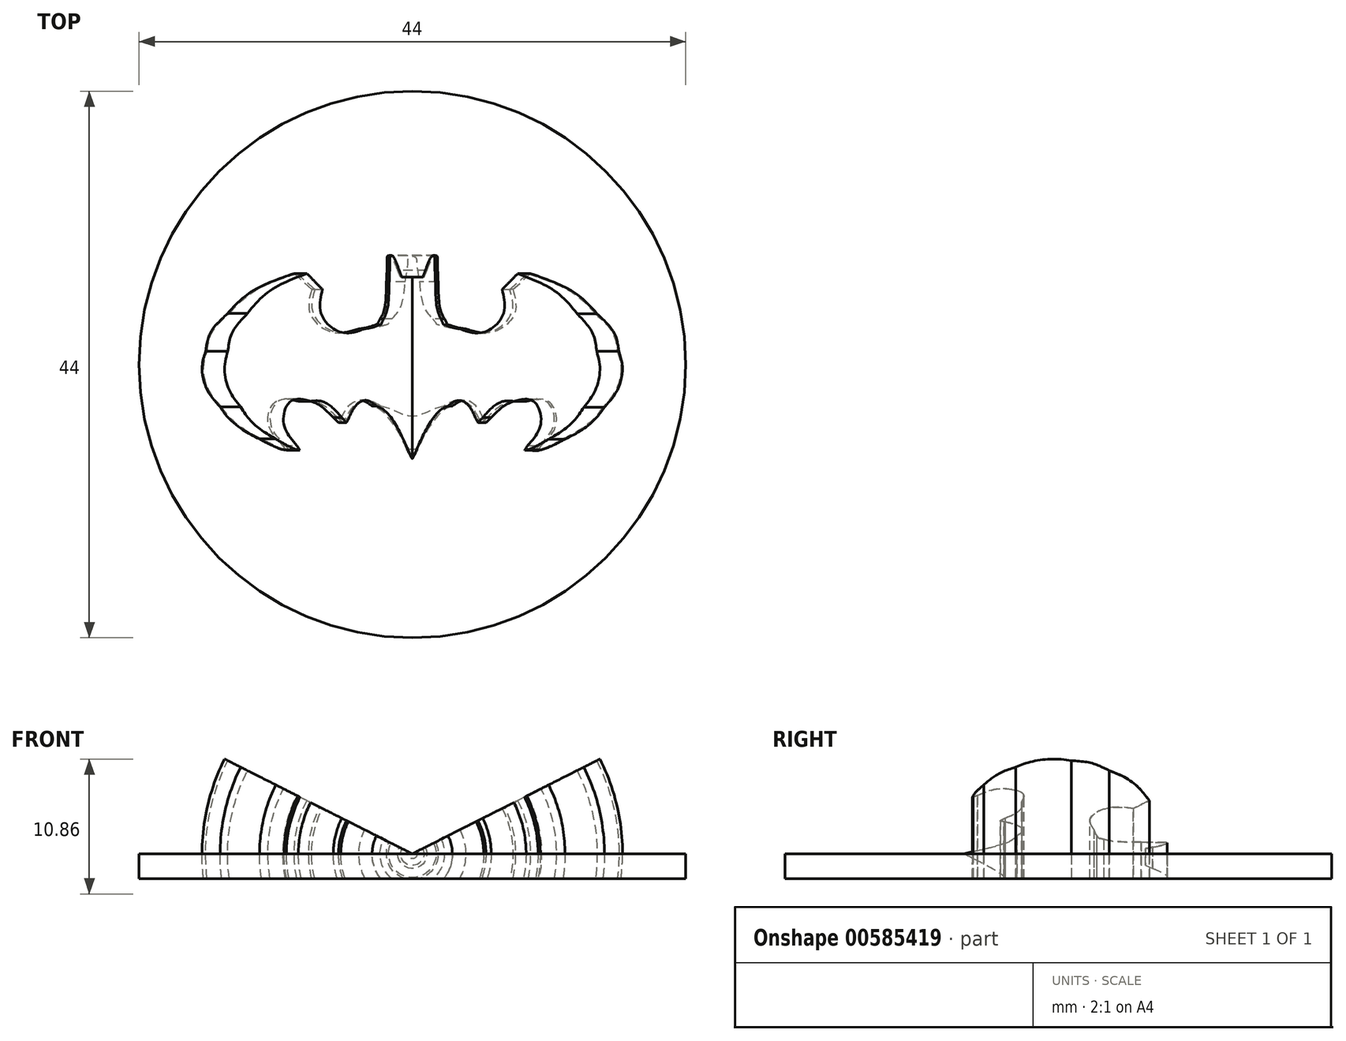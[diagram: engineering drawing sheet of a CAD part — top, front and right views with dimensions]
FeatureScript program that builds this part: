
annotation { "Feature Type Name" : "Feature", "Feature Type Description" : "" }
export const myFeature = defineFeature(function(context is Context, id is Id, definition is map)
    precondition{}
    {
        {
            var Q0;
            Q0=qCreatedBy(makeId("Top.planeOp"),FACE);
            var sketch = newSketch(context, id + "F0", { "sketchPlane" : qUnion([Q0])});
            skCircle(sketch, "E0", {"center": v(0, 0) * mm, "radius": 22 * mm});
            skSolve(sketch);
        }
        {
            var Q0;
            Q0=makeQuery(id+"F0.imprint","IMPRINT",FACE,{"disambiguationData":[TD([[makeQuery(id+"F0.imprint","IMPRINT",EDGE,{"derivedFrom":sQuery(id+"F0.wireOp",EDGE,"E0")}),1.0]])]});
            extrude(context, id + "F1", {"entities" : qUnion([Q0]), "depth" : 2 * mm, "offsetDistance" : 25 * mm});
        }
        {
            var Q0;
            Q0=makeQuery(id+"F1.opExtrude","CAP_FACE",FACE,{"disambiguationData":[OSD([sQuery(id+"F0.wireOp",EDGE,"E0")])],"isStart":false});
            var sketch = newSketch(context, id + "F2", { "sketchPlane" : qUnion([Q0])});
            skFitSpline(sketch, "E1", {"points": [v(-0.13, 10.66) * mm, v(-2.12, 10.65) * mm, v(-4.12, 10.46) * mm, v(-6.06, 10.08) * mm]});
            skFitSpline(sketch, "E2", {"points": [v(-6.06, 10.08) * mm, v(-12.64, 8.8) * mm, v(-17.56, 5.4) * mm, v(-18.46, 1.5) * mm]});
            skFitSpline(sketch, "E3", {"points": [v(-18.46, 1.5) * mm, v(-18.67, 0.6) * mm, v(-18.7, -0.04) * mm, v(-18.6, -0.8) * mm]});
            skFitSpline(sketch, "E4", {"points": [v(-18.6, -0.8) * mm, v(-18.34, -2.52) * mm, v(-17.58, -3.93) * mm, v(-16.12, -5.37) * mm]});
            skFitSpline(sketch, "E5", {"points": [v(-16.12, -5.37) * mm, v(-13.13, -8.34) * mm, v(-7.89, -10.27) * mm, v(-1.84, -10.64) * mm]});
            skFitSpline(sketch, "E6", {"points": [v(-1.84, -10.64) * mm, v(-0.97, -10.7) * mm, v(2.5, -10.62) * mm, v(3.31, -10.53) * mm]});
            skFitSpline(sketch, "E7", {"points": [v(3.31, -10.53) * mm, v(5.05, -10.33) * mm, v(5.92, -10.17) * mm, v(7.45, -9.8) * mm]});
            skFitSpline(sketch, "E8", {"points": [v(7.45, -9.8) * mm, v(14.92, -7.94) * mm, v(19.33, -3.65) * mm, v(18.58, 1.02) * mm]});
            skFitSpline(sketch, "E9", {"points": [v(18.58, 1.02) * mm, v(17.95, 4.88) * mm, v(13.66, 8.25) * mm, v(7.4, 9.79) * mm]});
            skFitSpline(sketch, "E10", {"points": [v(7.4, 9.79) * mm, v(5, 10.38) * mm, v(2.44, 10.67) * mm, v(-0.13, 10.66) * mm]});
            skFitSpline(sketch, "E11", {"points": [v(1.9, 8.75) * mm, v(1.97, 8.75) * mm, v(2.02, 8.14) * mm, v(2.07, 6.65) * mm]});
            skFitSpline(sketch, "E12", {"points": [v(2.07, 6.65) * mm, v(2.12, 5.3) * mm, v(2.3, 4.22) * mm, v(2.58, 3.66) * mm]});
            skFitSpline(sketch, "E13", {"points": [v(2.58, 3.66) * mm, v(2.8, 3.24) * mm, v(2.8, 3.24) * mm, v(3.23, 3.1) * mm]});
            skFitSpline(sketch, "E14", {"points": [v(3.23, 3.1) * mm, v(3.47, 3.01) * mm, v(3.95, 2.91) * mm, v(4.28, 2.87) * mm]});
            skFitSpline(sketch, "E15", {"points": [v(4.28, 2.87) * mm, v(6.43, 2.6) * mm, v(8.2, 4.07) * mm, v(8.1, 6.04) * mm]});
            skFitSpline(sketch, "E16", {"points": [v(7.51, 7.65) * mm, v(7.37, 7.83) * mm, v(7.26, 7.99) * mm, v(7.27, 8) * mm]});
            skFitSpline(sketch, "E17", {"points": [v(9.5, 7.32) * mm, v(11.86, 6.43) * mm, v(13.54, 5.42) * mm, v(14.86, 4.09) * mm]});
            skFitSpline(sketch, "E18", {"points": [v(14.86, 4.09) * mm, v(15.92, 3.03) * mm, v(16.39, 2.22) * mm, v(16.62, 1.06) * mm]});
            skFitSpline(sketch, "E19", {"points": [v(16.62, 1.06) * mm, v(16.91, -0.37) * mm, v(16.45, -2.13) * mm, v(15.45, -3.43) * mm]});
            skFitSpline(sketch, "E20", {"points": [v(15.45, -3.43) * mm, v(14.76, -4.33) * mm, v(13.52, -5.34) * mm, v(12.28, -6) * mm]});
            skFitSpline(sketch, "E21", {"points": [v(12.28, -6) * mm, v(11.69, -6.32) * mm, v(10.6, -6.8) * mm, v(10.3, -6.87) * mm]});
            skFitSpline(sketch, "E22", {"points": [v(10.38, -6.52) * mm, v(11.58, -4.76) * mm, v(10.95, -2.97) * mm, v(9.15, -2.96) * mm]});
            skFitSpline(sketch, "E23", {"points": [v(9.15, -2.96) * mm, v(8.22, -2.96) * mm, v(7.28, -3.4) * mm, v(6.34, -4.28) * mm]});
            skLineSegment(sketch, "E24", {"start": v(10.3, -6.87) * mm, "end": v(10.11, -6.92) * mm});
            skLineSegment(sketch, "E25", {"start": v(10.11, -6.92) * mm, "end": v(10.38, -6.52) * mm});
            skFitSpline(sketch, "E26", {"points": [v(5.74, -4.4) * mm, v(5.02, -3.26) * mm, v(4.13, -2.89) * mm, v(3.21, -3.35) * mm]});
            skFitSpline(sketch, "E27", {"points": [v(3.21, -3.35) * mm, v(2.4, -3.75) * mm, v(1.28, -5.15) * mm, v(0.38, -6.85) * mm]});
            skFitSpline(sketch, "E28", {"points": [v(0.38, -6.85) * mm, v(0.18, -7.24) * mm, v(0, -7.55) * mm, v(-0.02, -7.55) * mm]});
            skFitSpline(sketch, "E29", {"points": [v(-0.02, -7.55) * mm, v(-0.03, -7.55) * mm, v(-0.14, -7.36) * mm, v(-0.26, -7.11) * mm]});
            skFitSpline(sketch, "E30", {"points": [v(-0.26, -7.11) * mm, v(-1.2, -5.26) * mm, v(-2.36, -3.8) * mm, v(-3.23, -3.36) * mm]});
            skFitSpline(sketch, "E31", {"points": [v(-3.23, -3.36) * mm, v(-4.15, -2.9) * mm, v(-5, -3.23) * mm, v(-5.69, -4.28) * mm]});
            skLineSegment(sketch, "E32", {"start": v(6.34, -4.28) * mm, "end": v(5.92, -4.67) * mm});
            skLineSegment(sketch, "E33", {"start": v(5.92, -4.67) * mm, "end": v(5.74, -4.4) * mm});
            skFitSpline(sketch, "E34", {"points": [v(-6.43, -4.21) * mm, v(-7.34, -3.38) * mm, v(-8.18, -2.98) * mm, v(-9.08, -2.97) * mm]});
            skFitSpline(sketch, "E35", {"points": [v(-9.08, -2.97) * mm, v(-9.94, -2.97) * mm, v(-10.52, -3.28) * mm, v(-10.84, -3.94) * mm]});
            skFitSpline(sketch, "E36", {"points": [v(-10.84, -3.94) * mm, v(-11.19, -4.65) * mm, v(-11.05, -5.52) * mm, v(-10.44, -6.45) * mm]});
            skLineSegment(sketch, "E37", {"start": v(-5.69, -4.28) * mm, "end": v(-5.94, -4.67) * mm});
            skLineSegment(sketch, "E38", {"start": v(-5.94, -4.67) * mm, "end": v(-6.43, -4.21) * mm});
            skLineSegment(sketch, "E39", {"start": v(-6.43, -4.21) * mm, "end": v(-5.69, -4.28) * mm});
            skFitSpline(sketch, "E40", {"points": [v(-10.33, -6.87) * mm, v(-10.63, -6.8) * mm, v(-11.71, -6.32) * mm, v(-12.3, -6) * mm]});
            skFitSpline(sketch, "E41", {"points": [v(-12.3, -6) * mm, v(-14.06, -5.06) * mm, v(-15.44, -3.75) * mm, v(-16.14, -2.36) * mm]});
            skFitSpline(sketch, "E42", {"points": [v(-16.14, -2.36) * mm, v(-16.6, -1.42) * mm, v(-16.83, -0.11) * mm, v(-16.68, 0.85) * mm]});
            skFitSpline(sketch, "E43", {"points": [v(-16.68, 0.85) * mm, v(-16.58, 1.51) * mm, v(-16.24, 2.37) * mm, v(-15.86, 2.95) * mm]});
            skFitSpline(sketch, "E44", {"points": [v(-15.86, 2.95) * mm, v(-15.35, 3.73) * mm, v(-14.24, 4.78) * mm, v(-13.25, 5.44) * mm]});
            skFitSpline(sketch, "E45", {"points": [v(-13.25, 5.44) * mm, v(-12.1, 6.21) * mm, v(-10.63, 6.93) * mm, v(-9.1, 7.47) * mm]});
            skFitSpline(sketch, "E46", {"points": [v(-9.1, 7.47) * mm, v(-8.49, 7.7) * mm, v(-7.33, 8.03) * mm, v(-7.3, 8) * mm]});
            skFitSpline(sketch, "E47", {"points": [v(-7.3, 8) * mm, v(-7.28, 7.99) * mm, v(-7.39, 7.83) * mm, v(-7.53, 7.65) * mm]});
            skFitSpline(sketch, "E48", {"points": [v(-7.53, 7.65) * mm, v(-8.43, 6.5) * mm, v(-8.3, 4.8) * mm, v(-7.22, 3.77) * mm]});
            skFitSpline(sketch, "E49", {"points": [v(-7.22, 3.77) * mm, v(-6.42, 3) * mm, v(-5.3, 2.7) * mm, v(-4.08, 2.9) * mm]});
            skFitSpline(sketch, "E50", {"points": [v(-4.08, 2.9) * mm, v(-3.73, 2.96) * mm, v(-3.3, 3.06) * mm, v(-3.13, 3.12) * mm]});
            skFitSpline(sketch, "E51", {"points": [v(-3.13, 3.12) * mm, v(-2.84, 3.23) * mm, v(-2.8, 3.28) * mm, v(-2.61, 3.65) * mm]});
            skFitSpline(sketch, "E52", {"points": [v(-2.61, 3.65) * mm, v(-2.27, 4.35) * mm, v(-2.1, 5.52) * mm, v(-2.04, 7.63) * mm]});
            skFitSpline(sketch, "E53", {"points": [v(-2.04, 7.63) * mm, v(-2.03, 8.21) * mm, v(-2, 8.7) * mm, v(-1.98, 8.73) * mm]});
            skFitSpline(sketch, "E54", {"points": [v(-1.98, 8.73) * mm, v(-1.87, 8.84) * mm, v(-1.38, 8.11) * mm, v(-1.12, 7.46) * mm]});
            skLineSegment(sketch, "E55", {"start": v(-10.44, -6.45) * mm, "end": v(-10.14, -6.92) * mm});
            skLineSegment(sketch, "E56", {"start": v(-10.14, -6.92) * mm, "end": v(-10.33, -6.87) * mm});
            skLineSegment(sketch, "E57", {"start": v(-10.33, -6.87) * mm, "end": v(-10.44, -6.45) * mm});
            skFitSpline(sketch, "E58", {"points": [v(1.16, 7.58) * mm, v(1.4, 8.12) * mm, v(1.8, 8.75) * mm, v(1.9, 8.75) * mm]});
            skLineSegment(sketch, "E59", {"start": v(-1.12, 7.46) * mm, "end": v(-0.95, 7.02) * mm});
            skLineSegment(sketch, "E60", {"start": v(-0.95, 7.02) * mm, "end": v(0, 7.02) * mm});
            skLineSegment(sketch, "E61", {"start": v(0, 7.02) * mm, "end": v(0.93, 7.02) * mm});
            skLineSegment(sketch, "E62", {"start": v(0.93, 7.02) * mm, "end": v(1.16, 7.58) * mm});
            skLineSegment(sketch, "E63", {"start": v(-26.11, 0) * mm, "end": v(26.5, 0) * mm, "construction": true});
            skLineSegment(sketch, "E64", {"start": v(0, 7.02) * mm, "end": v(-0.02, -7.55) * mm});
            skLineSegment(sketch, "E65", {"start": v(8.1, 6.04) * mm, "end": v(9.5, 7.32) * mm});
            skSolve(sketch);
        }
        {
            var Q0;
            Q0=makeQuery(id+"F2.imprint","IMPRINT",FACE,{"disambiguationData":[TD([[makeQuery(id+"F2.imprint","IMPRINT",EDGE,{"derivedFrom":sQuery(id+"F2.wireOp",EDGE,"E11")}),-1.0]])]});
            var Q1;
            Q1=sQuery(id+"F2.wireOp",EDGE,"E64");
            revolve(context, id + "F3", {"entities" : qUnion([Q0]), "axis" : qUnion([Q1]), "revolveType" : RevolveType.SYMMETRIC, "angle" : 360 * degree});
        }
        {
            var Q0;
            Q0=qCreatedBy(makeId("Front.planeOp"),FACE);
            var sketch = newSketch(context, id + "F4", { "sketchPlane" : qUnion([Q0])});
            skLineSegment(sketch, "E66", {"start": v(-0.02, 2) * mm, "end": v(-22.6, 13.4) * mm});
            skLineSegment(sketch, "E67", {"start": v(-22.6, 13.4) * mm, "end": v(-22.6, 24.68) * mm});
            skLineSegment(sketch, "E68", {"start": v(22.57, 13.4) * mm, "end": v(-0.02, 2) * mm});
            skLineSegment(sketch, "E69", {"start": v(-0.02, 2) * mm, "end": v(-0.02, 27.64) * mm});
            skLineSegment(sketch, "E70", {"start": v(-22.6, 24.68) * mm, "end": v(22.8, 24.68) * mm});
            skLineSegment(sketch, "E71", {"start": v(22.8, 24.68) * mm, "end": v(22.57, 13.4) * mm});
            skLineSegment(sketch, "E72", {"start": v(-25.58, 0) * mm, "end": v(29.01, 0) * mm});
            skLineSegment(sketch, "E73", {"start": v(29.01, 0) * mm, "end": v(27.14, -13.54) * mm});
            skLineSegment(sketch, "E74", {"start": v(27.14, -13.54) * mm, "end": v(-17.5, -16.12) * mm});
            skLineSegment(sketch, "E75", {"start": v(-17.5, -16.12) * mm, "end": v(-25.58, 0) * mm});
            skSolve(sketch);
        }
        {
            var Q0;
            Q0 = qSketchRegion(id + "F4", true);
            extrude(context, id + "F5", {"entities" : qUnion([Q0]), "operationType" : NewBodyOperationType.REMOVE, "endBound" : BoundingType.SYMMETRIC, "depth" : 50 * mm, "offsetDistance" : 25 * mm});
        }
    });
